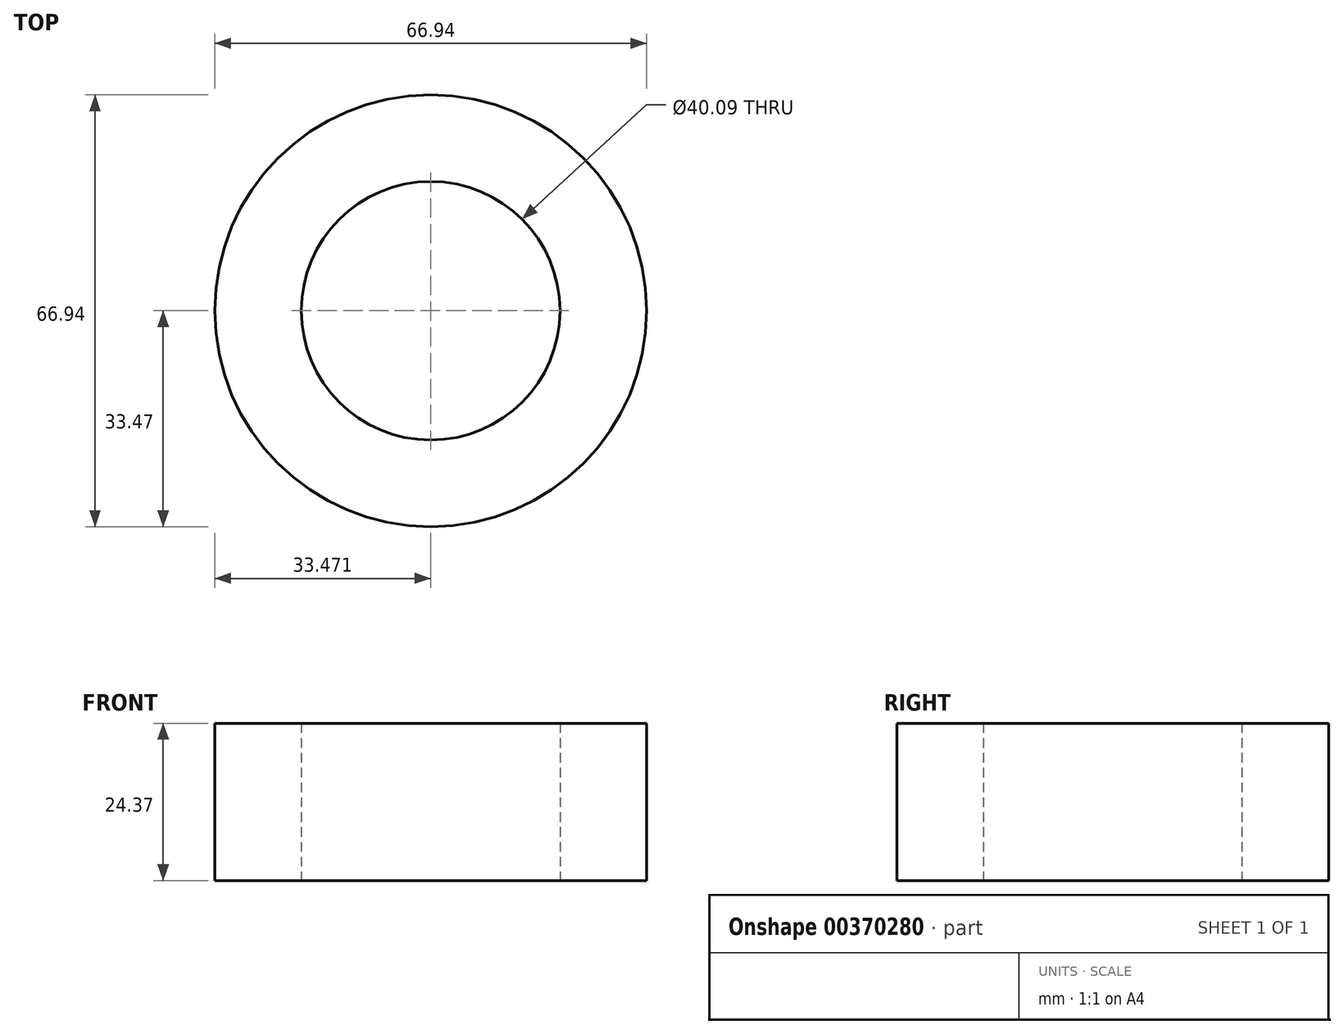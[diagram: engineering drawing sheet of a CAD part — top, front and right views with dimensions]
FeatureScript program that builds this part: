
annotation { "Feature Type Name" : "Feature", "Feature Type Description" : "" }
export const myFeature = defineFeature(function(context is Context, id is Id, definition is map)
    precondition{}
    {
        {
            var Q0;
            Q0=qCreatedBy(makeId("Front.planeOp"),FACE);
            var sketch = newSketch(context, id + "F0", { "sketchPlane" : qUnion([Q0])});
            skLineSegment(sketch, "E0", {"start": v(0, 0) * mm, "end": v(0, 24.37) * mm});
            skLineSegment(sketch, "E1", {"start": v(0, 24.37) * mm, "end": v(13.43, 24.37) * mm});
            skLineSegment(sketch, "E2", {"start": v(13.43, 24.37) * mm, "end": v(13.43, 0) * mm});
            skLineSegment(sketch, "E3", {"start": v(13.43, 0) * mm, "end": v(0, 0) * mm});
            skLineSegment(sketch, "E4.bottom", {"start": v(0, 4.13) * mm, "end": v(6.71, 4.13) * mm});
            skLineSegment(sketch, "E4.top", {"start": v(0, 0) * mm, "end": v(6.71, 0) * mm});
            skLineSegment(sketch, "E4.left", {"start": v(0, 4.13) * mm, "end": v(0, 0) * mm});
            skLineSegment(sketch, "E4.right", {"start": v(6.71, 4.13) * mm, "end": v(6.71, 0) * mm});
            skArc(sketch, "E5", {"start": v(0, 7.85) * mm, "mid": v(7.02, 14.87) * mm, "end": v(0, 21.9) * mm});
            skLineSegment(sketch, "E6", {"start": v(33.47, 0) * mm, "end": v(33.47, 24.37) * mm});
            skSolve(sketch);
        }
        {
            var Q0;
            Q0 = qSketchRegion(id + "F0", true);
            var Q1;
            Q1=sQuery(id+"F0.wireOp",EDGE,"E6");
            revolve(context, id + "F1", {"entities" : qUnion([Q0]), "axis" : qUnion([Q1]), "revolveType" : RevolveType.FULL});
        }
    });
